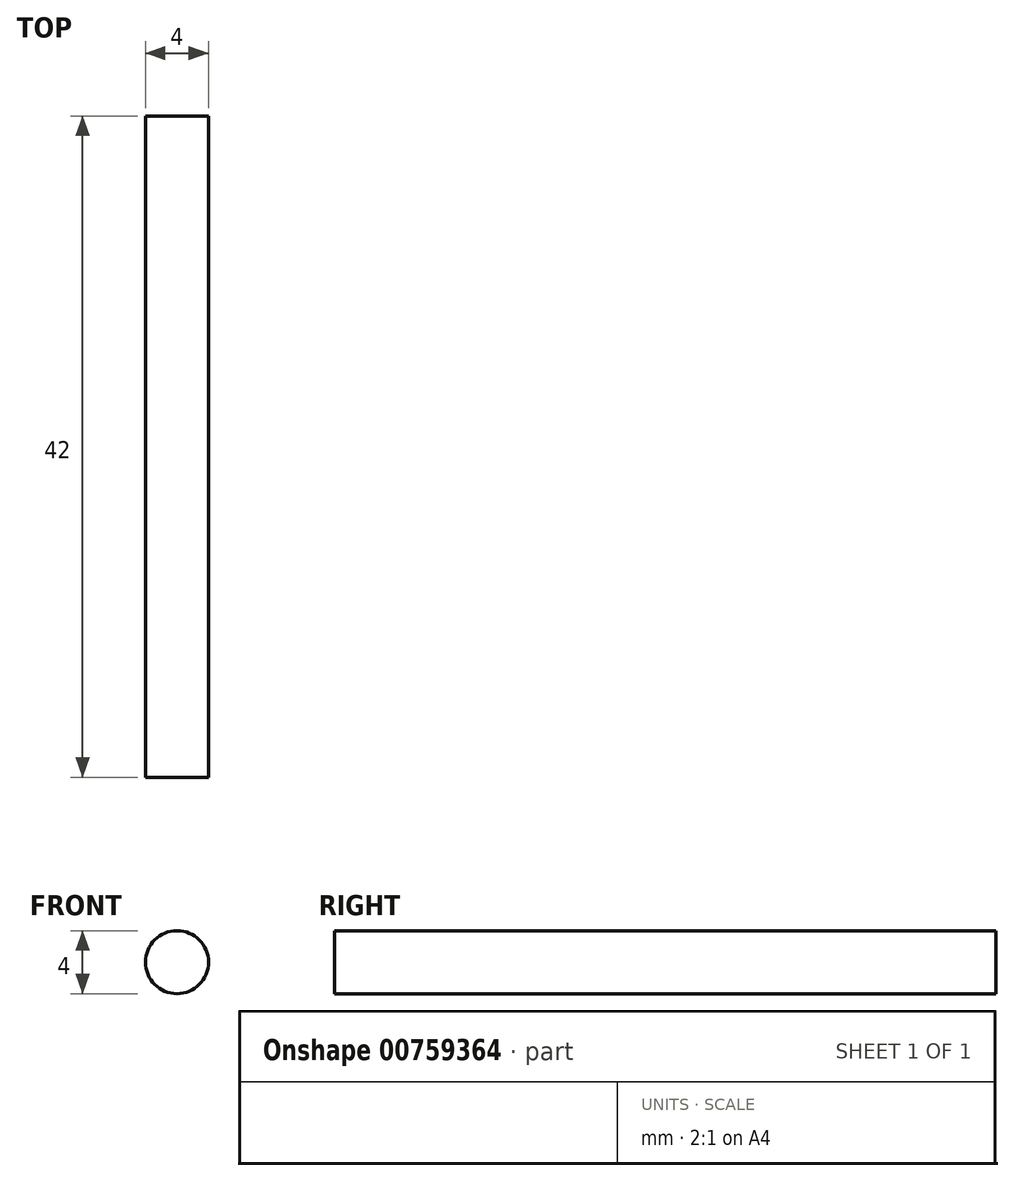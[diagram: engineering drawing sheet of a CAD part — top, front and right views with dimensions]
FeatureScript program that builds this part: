
annotation { "Feature Type Name" : "Feature", "Feature Type Description" : "" }
export const myFeature = defineFeature(function(context is Context, id is Id, definition is map)
    precondition{}
    {
        {
            var Q0;
            Q0=qCreatedBy(makeId("Front.planeOp"),FACE);
            var sketch = newSketch(context, id + "F0", { "sketchPlane" : qUnion([Q0])});
            skCircle(sketch, "E0", {"center": v(8.05, 4.81) * mm, "radius": 2 * mm});
            skSolve(sketch);
        }
        {
            var Q0;
            Q0 = qSketchRegion(id + "F0", true);
            extrude(context, id + "F1", {"entities" : qUnion([Q0]), "depth" : 42 * mm, "offsetDistance" : 25 * mm});
        }
    });
